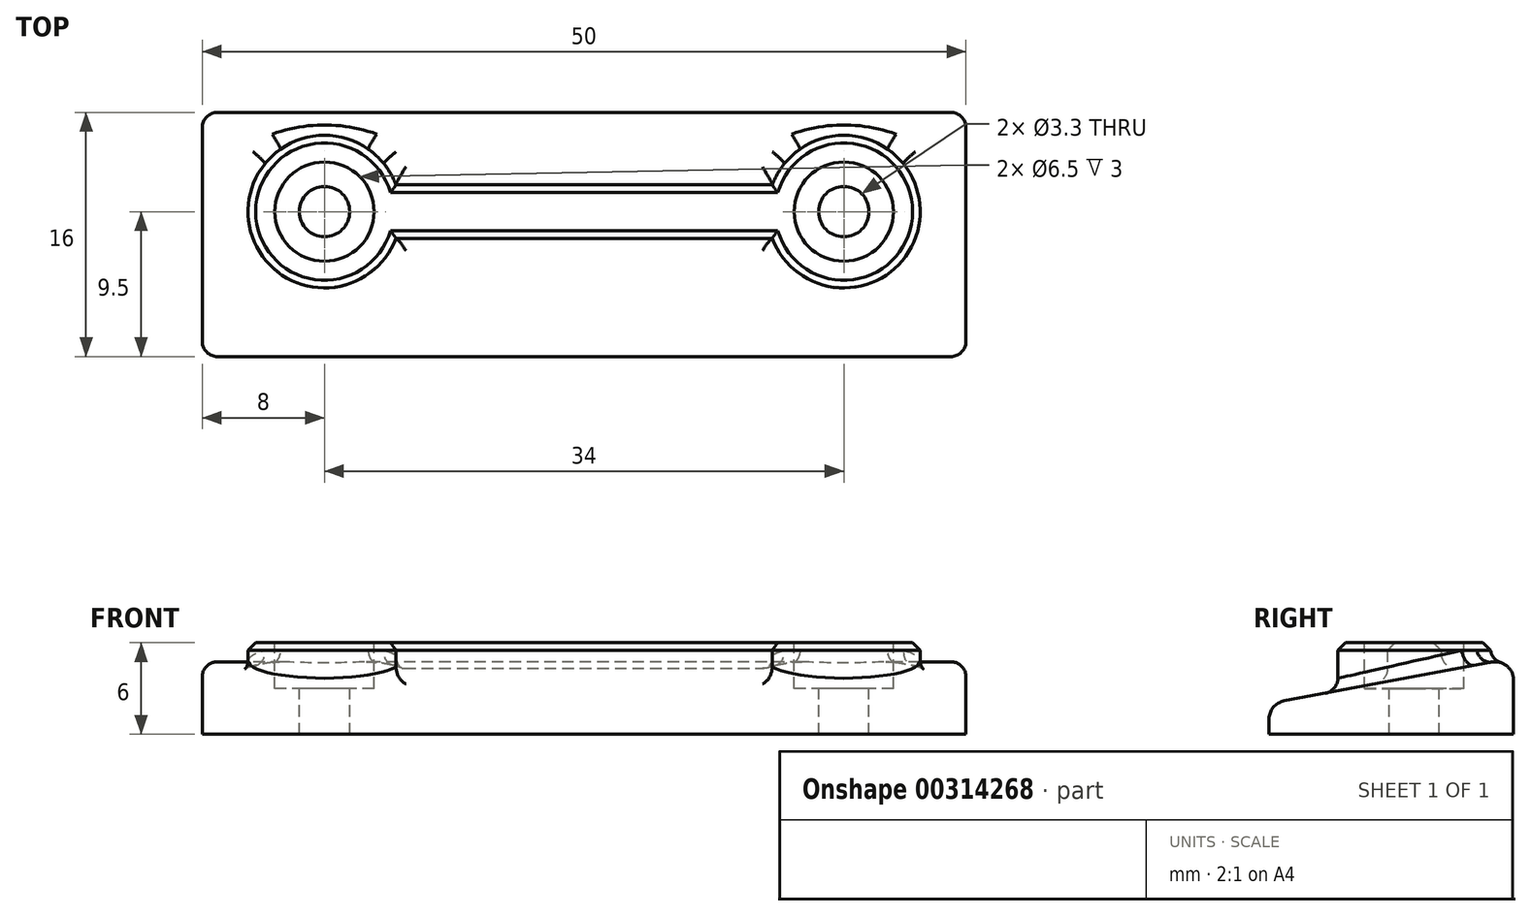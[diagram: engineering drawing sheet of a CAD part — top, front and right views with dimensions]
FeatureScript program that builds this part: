
annotation { "Feature Type Name" : "Feature", "Feature Type Description" : "" }
export const myFeature = defineFeature(function(context is Context, id is Id, definition is map)
    precondition{}
    {
        {
            var Q0;
            Q0=qCreatedBy(makeId("Right.planeOp"),FACE);
            var sketch = newSketch(context, id + "F0", { "sketchPlane" : qUnion([Q0])});
            skLineSegment(sketch, "E0", {"start": v(0, 0) * mm, "end": v(-16, 0) * mm});
            skLineSegment(sketch, "E1", {"start": v(-16, 0) * mm, "end": v(-16, 1) * mm});
            skLineSegment(sketch, "E2", {"start": v(-15.02, 2.18) * mm, "end": v(-1.42, 4.73) * mm});
            skLineSegment(sketch, "E3", {"start": v(0, 3.55) * mm, "end": v(0, 0) * mm});
            skPoint(sketch, "E4.visualSharp", {"position": v(-16, 2) * mm});
            skArc(sketch, "E4.filletArc", {"start": v(-15.02, 2.18) * mm, "mid": v(-15.72, 1.77) * mm, "end": v(-16, 1) * mm});
            skPoint(sketch, "E5.visualSharp", {"position": v(0, 5) * mm});
            skArc(sketch, "E5.filletArc", {"start": v(0, 3.55) * mm, "mid": v(-0.43, 4.48) * mm, "end": v(-1.42, 4.73) * mm});
            skSolve(sketch);
        }
        {
            var Q0;
            Q0 = qSketchRegion(id + "F0", true);
            extrude(context, id + "F1", {"entities" : qUnion([Q0]), "depth" : 50 * mm});
        }
        {
            var Q0;
            Q0=makeQuery(id+"F1.opExtrude","SWEPT_FACE",FACE,{"disambiguationData":[OSD([sQuery(id+"F0.wireOp",EDGE,"E0")])]});
            var sketch = newSketch(context, id + "F2", { "sketchPlane" : qUnion([Q0])});
            skLineSegment(sketch, "E6", {"start": v(0, 6.5) * mm, "end": v(50, 6.5) * mm, "construction": true});
            skLineSegment(sketch, "E7", {"start": v(25, 6.5) * mm, "end": v(25, 16) * mm, "construction": true});
            skArc(sketch, "E8", {"start": v(12.68, 8.25) * mm, "mid": v(3, 6.5) * mm, "end": v(12.68, 4.75) * mm});
            skArc(sketch, "E9", {"start": v(37.32, 4.75) * mm, "mid": v(47, 6.5) * mm, "end": v(37.32, 8.25) * mm});
            skLineSegment(sketch, "E10.0", {"start": v(12.68, 4.75) * mm, "end": v(37.32, 4.75) * mm});
            skLineSegment(sketch, "E11.0", {"start": v(12.68, 8.25) * mm, "end": v(37.32, 8.25) * mm});
            skSolve(sketch);
        }
        {
            var Q0;
            Q0 = qSketchRegion(id + "F2", true);
            extrude(context, id + "F3", {"entities" : qUnion([Q0]), "operationType" : NewBodyOperationType.ADD, "oppositeDirection" : true, "depth" : 6 * mm});
        }
        {
            var Q0;
            Q0=makeQuery(id+"F3.opExtrude","CAP_FACE",FACE,{"disambiguationData":[OSD([sQuery(id+"F2.wireOp",EDGE,"E8"),sQuery(id+"F2.wireOp",EDGE,"E9"),sQuery(id+"F2.wireOp",EDGE,"E10.0"),sQuery(id+"F2.wireOp",EDGE,"E11.0")])],"isStart":false});
            chamfer(context, id + "F4", {"entities" : qUnion([Q0]), "width" : 0.5 * mm, "tangentPropagation" : true});
        }
        {
            var Q0;
            Q0=makeQuery(id+"F3.opExtrude","CAP_FACE",FACE,{"disambiguationData":[OSD([sQuery(id+"F2.wireOp",EDGE,"E8"),sQuery(id+"F2.wireOp",EDGE,"E9"),sQuery(id+"F2.wireOp",EDGE,"E10.0"),sQuery(id+"F2.wireOp",EDGE,"E11.0")])],"isStart":false});
            var sketch = newSketch(context, id + "F5", { "sketchPlane" : qUnion([Q0])});
            skPoint(sketch, "E12", {"position": v(8, -6.5) * mm});
            skPoint(sketch, "E13", {"position": v(42, -6.5) * mm});
            skSolve(sketch);
        }
        {
            var Q0;
            Q0=sQuery(id+"F5.wireOp",VERTEX,"E12");
            var Q1;
            Q1=sQuery(id+"F5.wireOp",VERTEX,"E13");
            var Q2;
            Q2=makeQuery(id+"F1.opExtrude","SWEPT_BODY",BODY,{"disambiguationData":[OSD([sQuery(id+"F0.wireOp",EDGE,"E0"),sQuery(id+"F0.wireOp",EDGE,"E1"),sQuery(id+"F0.wireOp",EDGE,"E2"),sQuery(id+"F0.wireOp",EDGE,"E3"),sQuery(id+"F0.wireOp",EDGE,"E4.filletArc"),sQuery(id+"F0.wireOp",EDGE,"E5.filletArc")])]});
            hole(context, id + "F6", {"style" : HoleStyle.C_BORE, "endStyle" : HoleEndStyle.THROUGH, "standardTappedOrClearance" : lookupTablePath({ "standard" : "ISO", "fit" : "Normal", "size" : "M3", "type" : "Clearance" }), "standardBlindInLast" : lookupTablePath({ "fit" : "Standard", "standard" : "ISO", "size" : "M3", "type" : "Clearance" }), "holeDiameter" : 3.3 * mm, "cBoreDiameter" : 6.5 * mm, "cBoreDepth" : 3 * mm, "tappedDepth" : 3 * mm, "tapClearance" : 3, "startFromSketch" : true, "locations" : qUnion([Q0, Q1]), "scope" : qUnion([Q2])});
        }
        {
            var Q0;
            Q0=makeQuery(id+"F3.boolean.opBoolean","INTERSECT",EDGE,{"derivedFrom":[makeQuery(id+"F1.opExtrude","SWEPT_FACE",FACE,{"disambiguationData":[OSD([sQuery(id+"F0.wireOp",EDGE,"E2")])]}),makeQuery(id+"F3.opExtrude","SWEPT_FACE",FACE,{"disambiguationData":[OSD([sQuery(id+"F2.wireOp",EDGE,"E11.0")])]})]});
            var Q1;
            Q1=makeQuery(id+"F3.boolean.opBoolean","INTERSECT",EDGE,{"derivedFrom":[makeQuery(id+"F1.opExtrude","SWEPT_FACE",FACE,{"disambiguationData":[OSD([sQuery(id+"F0.wireOp",EDGE,"E2")])]}),makeQuery(id+"F3.opExtrude","SWEPT_FACE",FACE,{"disambiguationData":[OSD([sQuery(id+"F2.wireOp",EDGE,"E9")])]})]});
            var Q2;
            Q2=makeQuery(id+"F3.boolean.opBoolean","INTERSECT",EDGE,{"derivedFrom":[makeQuery(id+"F1.opExtrude","SWEPT_FACE",FACE,{"disambiguationData":[OSD([sQuery(id+"F0.wireOp",EDGE,"E2")])]}),makeQuery(id+"F3.opExtrude","SWEPT_FACE",FACE,{"disambiguationData":[OSD([sQuery(id+"F2.wireOp",EDGE,"E8")])]})]});
            var Q3;
            Q3=makeQuery(id+"F3.boolean.opBoolean","INTERSECT",EDGE,{"derivedFrom":[makeQuery(id+"F1.opExtrude","SWEPT_FACE",FACE,{"disambiguationData":[OSD([sQuery(id+"F0.wireOp",EDGE,"E2")])]}),makeQuery(id+"F3.opExtrude","SWEPT_FACE",FACE,{"disambiguationData":[OSD([sQuery(id+"F2.wireOp",EDGE,"E10.0")])]})]});
            fillet(context, id + "F7", {"entities" : qUnion([Q0, Q1, Q2, Q3]), "radius" : 1 * mm, "tangentPropagation" : true, "allowEdgeOverflow" : false});
        }
        {
            var Q0;
            Q0=makeQuery(id+"F1.opExtrude","CAP_EDGE",EDGE,{"disambiguationData":[OSD([sQuery(id+"F0.wireOp",EDGE,"E2")])],"isStart":false});
            var Q1;
            Q1=makeQuery(id+"F1.opExtrude","CAP_EDGE",EDGE,{"disambiguationData":[OSD([sQuery(id+"F0.wireOp",EDGE,"E2")])],"isStart":true});
            fillet(context, id + "F8", {"entities" : qUnion([Q0, Q1]), "radius" : 1 * mm, "tangentPropagation" : true, "allowEdgeOverflow" : false});
        }
    });
